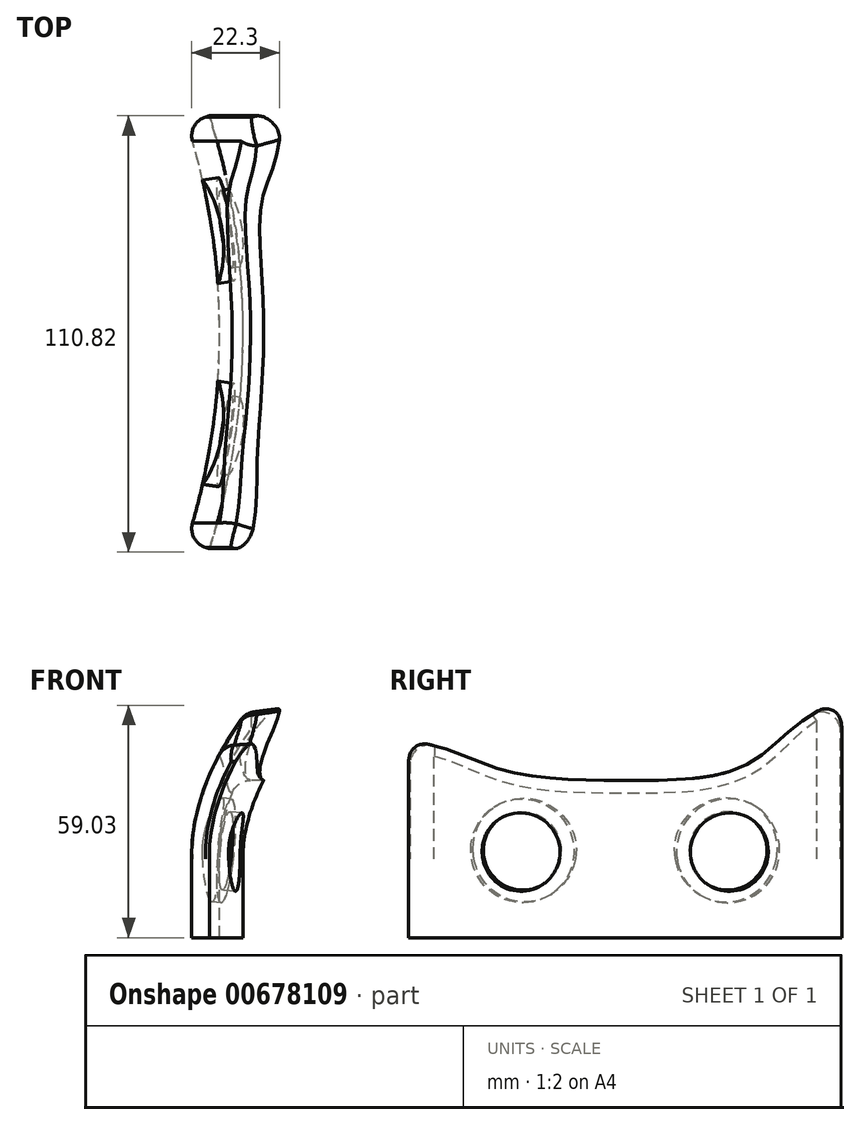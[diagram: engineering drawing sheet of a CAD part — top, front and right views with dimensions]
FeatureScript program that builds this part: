
annotation { "Feature Type Name" : "Feature", "Feature Type Description" : "" }
export const myFeature = defineFeature(function(context is Context, id is Id, definition is map)
    precondition{}
    {
        {
            var Q0;
            Q0=qCreatedBy(makeId("Top.planeOp"),FACE);
            var sketch = newSketch(context, id + "F0", { "sketchPlane" : qUnion([Q0])});
            skCircle(sketch, "E0", {"center": v(0, 0) * mm, "radius": 175 * mm});
            skCircle(sketch, "E1", {"center": v(0, 0) * mm, "radius": 181 * mm});
            skLineSegment(sketch, "E2", {"start": v(0, 0) * mm, "end": v(172.44, 55) * mm});
            skLineSegment(sketch, "E3", {"start": v(0, 0) * mm, "end": v(172.44, -55) * mm});
            skLineSegment(sketch, "E4", {"start": v(172.44, -55) * mm, "end": v(172.44, 55) * mm, "construction": true});
            skPoint(sketch, "E5", {"position": v(175, 0) * mm});
            skLineSegment(sketch, "E6", {"start": v(0, 0) * mm, "end": v(223.4, 0) * mm, "construction": true});
            skPoint(sketch, "E6.endSnap0", {"position": v(172.44, 0) * mm});
            skLineSegment(sketch, "E7", {"start": v(0, 0) * mm, "end": v(293.26, 43.83) * mm, "construction": true});
            skLineSegment(sketch, "E8", {"start": v(0, 0) * mm, "end": v(282.96, -42.29) * mm, "construction": true});
            skLineSegment(sketch, "E9", {"start": v(0, 0) * mm, "end": v(-12.67, 84.8) * mm, "construction": true});
            skLineSegment(sketch, "E10", {"start": v(0, 0) * mm, "end": v(13.6, 91) * mm, "construction": true});
            skSolve(sketch);
        }
        {
            var Q0;
            Q0=qCreatedBy(makeId("Front.planeOp"),FACE);
            var sketch = newSketch(context, id + "F1", { "sketchPlane" : qUnion([Q0])});
            skLineSegment(sketch, "E11.0", {"start": v(-175, 0) * mm, "end": v(175, 0) * mm, "construction": true});
            skLineSegment(sketch, "E12.0", {"start": v(-181, 0) * mm, "end": v(181, 0) * mm, "construction": true});
            skPoint(sketch, "E13.0", {"position": v(172.44, 0) * mm});
            skLineSegment(sketch, "E14", {"start": v(175, 0) * mm, "end": v(181, 0) * mm, "construction": true});
            skPoint(sketch, "E15", {"position": v(178, 0) * mm});
            skFitSpline(sketch, "E16", {"points": [v(178, 0) * mm, v(178, 1.47) * mm, v(203, 45) * mm], "startDerivative": vector(0, 25) * mm, "endDerivative": vector(87.82, 75.46) * mm});
            skLineSegment(sketch, "E17", {"start": v(178, 0) * mm, "end": v(178, 47.04) * mm, "construction": true});
            skLineSegment(sketch, "E18", {"start": v(178, 0) * mm, "end": v(178, -20) * mm, "construction": true});
            skLineSegment(sketch, "E19", {"start": v(178, -20) * mm, "end": v(203, 45) * mm, "construction": true});
            skLineSegment(sketch, "E20", {"start": v(200.37, 20.25) * mm, "end": v(154.68, 20.25) * mm, "construction": true});
            skLineSegment(sketch, "E21", {"start": v(183, 20.25) * mm, "end": v(178, -20) * mm, "construction": true});
            skLineSegment(sketch, "E22", {"start": v(180.5, 0.13) * mm, "end": v(0, 69.55) * mm, "construction": true});
            skLineSegment(sketch, "E23", {"start": v(181, 0) * mm, "end": v(0, 22.5) * mm, "construction": true});
            skLineSegment(sketch, "E24", {"start": v(0, 0) * mm, "end": v(0, 135) * mm, "construction": true});
            skLineSegment(sketch, "E25", {"start": v(0, 0) * mm, "end": v(10.2, 105.85) * mm, "construction": true});
            skLineSegment(sketch, "E26", {"start": v(0, 0) * mm, "end": v(40.9, 106.32) * mm, "construction": true});
            skSolve(sketch);
        }
        {
            var Q0;
            {var subQ0=sQuery(id+"F0.wireOp",EDGE,"E2");var subQ1=sQuery(id+"F0.wireOp",EDGE,"E0");var subQ2=makeQuery(id+"F0.imprint","INTERSECT",VERTEX,{"derivedFrom":[subQ1,subQ0]});Q0=makeQuery(id+"F0.imprint","IMPRINT",FACE,{"disambiguationData":[TD([[makeQuery(id+"F0.imprint","IMPRINT",EDGE,{"disambiguationData":[TD([[subQ2,1.0]])],"derivedFrom":subQ1}),-1.0]])]});}
            var Q1;
            Q1=sQuery(id+"F1.wireOp",EDGE,"E16");
            sweep(context, id + "F2", {"profiles" : qUnion([Q0]), "path" : qUnion([Q1])});
        }
        {
            var Q0;
            Q0=makeQuery(id+"F2.opSweep","SWEPT_EDGE",EDGE,{"disambiguationData":[OSD([sQuery(id+"F0.wireOp",EDGE,"E1"),sQuery(id+"F0.wireOp",EDGE,"E3"),sQuery(id+"F1.wireOp",EDGE,"E16")])]});
            cPoint(context, id + "F3", {"entities" : qUnion([Q0]), "parameter" : 0.5});
        }
        {
            var Q0;
            Q0=qCreatedBy(makeId("Front.planeOp"),FACE);
            var Q1;
            Q1=qCreatedBy(id+"F3",VERTEX);
            cPlane(context, id + "F4", {"entities" : qUnion([Q0, Q1]), "cplaneType" : CPlaneType.PLANE_POINT, "offset" : 25 * mm, "width" : 150 * mm, "height" : 150 * mm});
        }
        {
            var Q0;
            Q0=qCreatedBy(id+"F4.planeOp",FACE);
            var sketch = newSketch(context, id + "F5", { "sketchPlane" : qUnion([Q0])});
            skLineSegment(sketch, "E27", {"start": v(16.14, 30) * mm, "end": v(342.74, 30) * mm});
            skLineSegment(sketch, "E28.top", {"start": v(16.14, 180) * mm, "end": v(342.74, 180) * mm});
            skLineSegment(sketch, "E28.left", {"start": v(16.14, 30) * mm, "end": v(16.14, 180) * mm});
            skLineSegment(sketch, "E28.right", {"start": v(342.74, 30) * mm, "end": v(342.74, 180) * mm});
            skSolve(sketch);
        }
        {
            var Q0;
            Q0=qCreatedBy(makeId("Right.planeOp"),FACE);
            var sketch = newSketch(context, id + "F6", { "sketchPlane" : qUnion([Q0])});
            skPoint(sketch, "E29.0", {"position": v(-55, 30) * mm});
            skLineSegment(sketch, "E30", {"start": v(-74, 30) * mm, "end": v(-141.5, 30) * mm, "construction": true});
            skFitSpline(sketch, "E31.0", {"points": [v(55, 0) * mm, v(1000, 55) * mm, v(1.76, 1000) * mm, v(55, 1.45) * mm, v(1000, 55) * mm, v(2.22, 1000) * mm, v(55, 2.64) * mm, v(1000, 55) * mm, v(3.74, 1000) * mm, v(55, 4.43) * mm, v(1000, 55) * mm, v(6.86, 1000) * mm, v(55, 8.96) * mm, v(1000, 55) * mm, v(16.48, 1000) * mm, v(55, 23.08) * mm], "construction": true});
            skFitSpline(sketch, "E32.0", {"points": [v(-55, 0) * mm, v(1000, -55) * mm, v(1.76, 1000) * mm, v(-55, 1.45) * mm, v(1000, -55) * mm, v(2.22, 1000) * mm, v(-55, 2.64) * mm, v(1000, -55) * mm, v(3.74, 1000) * mm, v(-55, 4.43) * mm, v(1000, -55) * mm, v(6.86, 1000) * mm, v(-55, 8.96) * mm, v(1000, -55) * mm, v(16.48, 1000) * mm, v(-55, 23.08) * mm], "construction": true});
            skLineSegment(sketch, "E33", {"start": v(68.45, 40) * mm, "end": v(-5.43, 40) * mm, "construction": true});
            skLineSegment(sketch, "E34", {"start": v(28.07, 20) * mm, "end": v(-24.08, 20) * mm, "construction": true});
            skFitSpline(sketch, "E35", {"points": [v(55, 40) * mm, v(31.56, 24.33) * mm, v(0, 20) * mm, v(-30.54, 22.45) * mm, v(-55, 30) * mm], "startDerivative": vector(-142.73, -39.4) * mm, "endDerivative": vector(-137.35, 16.17) * mm});
            skSolve(sketch);
        }
        {
            var Q0;
            Q0=makeQuery(id+"F5.imprint","IMPRINT",FACE,{"disambiguationData":[TD([[makeQuery(id+"F5.imprint","IMPRINT",EDGE,{"derivedFrom":sQuery(id+"F5.wireOp",EDGE,"E27")}),1.0]])]});
            var Q1;
            Q1=sQuery(id+"F6.wireOp",EDGE,"E35");
            sweep(context, id + "F7", {"operationType" : NewBodyOperationType.REMOVE, "profiles" : qUnion([Q0]), "path" : qUnion([Q1]), "keepProfileOrientation" : true});
        }
        {
            var Q0;
            Q0=makeQuery(id+"F7.boolean.opBoolean","INTERSECT",EDGE,{"derivedFrom":[makeQuery(id+"F2.opSweep","SWEPT_FACE",FACE,{"disambiguationData":[OSD([sQuery(id+"F0.wireOp",EDGE,"E0"),sQuery(id+"F1.wireOp",EDGE,"E16")])]}),makeQuery(id+"F7.opSweep","SWEPT_FACE",FACE,{"disambiguationData":[OSD([sQuery(id+"F5.wireOp",EDGE,"E27"),sQuery(id+"F6.wireOp",EDGE,"E35")])]})]});
            fillet(context, id + "F8", {"entities" : qUnion([Q0]), "radius" : 5 * mm, "tangentPropagation" : true, "allowEdgeOverflow" : false});
        }
        {
            var Q0;
            Q0=makeQuery(id+"F2.opSweep","SWEPT_EDGE",EDGE,{"disambiguationData":[OSD([sQuery(id+"F0.wireOp",EDGE,"E0"),sQuery(id+"F0.wireOp",EDGE,"E2"),sQuery(id+"F1.wireOp",EDGE,"E16")])]});
            var Q1;
            Q1=makeQuery(id+"F2.opSweep","SWEPT_EDGE",EDGE,{"disambiguationData":[OSD([sQuery(id+"F0.wireOp",EDGE,"E0"),sQuery(id+"F0.wireOp",EDGE,"E3"),sQuery(id+"F1.wireOp",EDGE,"E16")])]});
            fillet(context, id + "F9", {"entities" : qUnion([Q0, Q1]), "radius" : 5 * mm, "tangentPropagation" : true, "allowEdgeOverflow" : false});
        }
        {
            var Q0;
            Q0=makeQuery(id+"F2.opSweep","CAP_FACE",FACE,{"disambiguationData":[OSD([sQuery(id+"F0.wireOp",EDGE,"E0"),sQuery(id+"F0.wireOp",EDGE,"E1"),sQuery(id+"F0.wireOp",EDGE,"E2"),sQuery(id+"F0.wireOp",EDGE,"E3"),sQuery(id+"F1.wireOp",VERTEX,"E16.start")])],"isStart":true});
            var sketch = newSketch(context, id + "F10", { "sketchPlane" : qUnion([Q0])});
            skLineSegment(sketch, "E36.0.0", {"start": v(172.44, 55) * mm, "end": v(171.42, 54.68) * mm});
            skArc(sketch, "E36.0.1", {"start": v(171.42, 54.68) * mm, "mid": v(168.53, 52.27) * mm, "end": v(168.14, 48.53) * mm});
            skArc(sketch, "E36.0.2", {"start": v(168.14, -48.53) * mm, "mid": v(175, 0) * mm, "end": v(168.14, 48.53) * mm});
            skArc(sketch, "E36.0.3", {"start": v(168.14, -48.53) * mm, "mid": v(168.53, -52.27) * mm, "end": v(171.42, -54.68) * mm});
            skLineSegment(sketch, "E36.0.4", {"start": v(172.44, -55) * mm, "end": v(171.42, -54.68) * mm});
            skArc(sketch, "E36.0.5", {"start": v(172.44, -55) * mm, "mid": v(181, 0) * mm, "end": v(172.44, 55) * mm});
            skSolve(sketch);
        }
        {
            var Q0;
            Q0=makeQuery(id+"F10.imprint","IMPRINT",FACE,{"disambiguationData":[TD([[makeQuery(id+"F10.imprint","IMPRINT",EDGE,{"derivedFrom":sQuery(id+"F10.wireOp",EDGE,"E36.0.0")}),-1.0]])]});
            extrude(context, id + "F11", {"entities" : qUnion([Q0]), "operationType" : NewBodyOperationType.ADD, "depth" : 20 * mm, "offsetDistance" : 25 * mm, "hasSecondDirection" : true, "secondDirectionOppositeDirection" : true, "secondDirectionDepth" : 1 * mm});
        }
        {
            var Q0;
            Q0=sQuery(id+"F0.wireOp",VERTEX,"E9.end");
            var Q1;
            Q1=sQuery(id+"F0.wireOp",VERTEX,"E2.start");
            var Q2;
            Q2=sQuery(id+"F1.wireOp",VERTEX,"E25.end");
            cPlane(context, id + "F12", {"entities" : qUnion([Q0, Q1, Q2]), "cplaneType" : CPlaneType.THREE_POINT, "offset" : 25 * mm, "width" : 150 * mm, "height" : 150 * mm});
        }
        {
            var Q0;
            Q0=sQuery(id+"F0.wireOp",VERTEX,"E10.end");
            var Q1;
            Q1=sQuery(id+"F1.wireOp",VERTEX,"E25.end");
            var Q2;
            Q2=sQuery(id+"F0.wireOp",VERTEX,"E2.start");
            cPlane(context, id + "F13", {"entities" : qUnion([Q0, Q1, Q2]), "cplaneType" : CPlaneType.THREE_POINT, "offset" : 25 * mm, "width" : 150 * mm, "height" : 150 * mm});
        }
        {
            var Q0;
            Q0=qCreatedBy(id+"F12.planeOp",FACE);
            var sketch = newSketch(context, id + "F14", { "sketchPlane" : qUnion([Q0])});
            skCircle(sketch, "E37", {"center": v(0, 19) * mm, "radius": 10 * mm});
            skCircle(sketch, "E38", {"center": v(0, 19) * mm, "radius": 13.25 * mm});
            skSolve(sketch);
        }
        {
            var Q0;
            Q0=qCreatedBy(id+"F13.planeOp",FACE);
            var sketch = newSketch(context, id + "F15", { "sketchPlane" : qUnion([Q0])});
            skCircle(sketch, "E39", {"center": v(0, 19) * mm, "radius": 10 * mm});
            skCircle(sketch, "E40", {"center": v(0, 19) * mm, "radius": 13.25 * mm});
            skSolve(sketch);
        }
        {
            var Q0;
            Q0=makeQuery(id+"F14.imprint","IMPRINT",FACE,{"disambiguationData":[TD([[makeQuery(id+"F14.imprint","IMPRINT",EDGE,{"derivedFrom":sQuery(id+"F14.wireOp",EDGE,"E37")}),1.0]])]});
            var Q1;
            Q1=makeQuery(id+"F2.opSweep","SWEPT_BODY",BODY,{"disambiguationData":[OSD([sQuery(id+"F0.wireOp",EDGE,"E0"),sQuery(id+"F0.wireOp",EDGE,"E1"),sQuery(id+"F0.wireOp",EDGE,"E2"),sQuery(id+"F0.wireOp",EDGE,"E3"),sQuery(id+"F1.wireOp",EDGE,"E16")])]});
            extrude(context, id + "F16", {"entities" : qUnion([Q0]), "operationType" : NewBodyOperationType.REMOVE, "endBound" : BoundingType.UP_TO_BODY, "depth" : 25 * mm, "endBoundEntityBody" : qUnion([Q1]), "hasOffset" : true, "offsetDistance" : 10 * mm, "offsetOppositeDirection" : true});
        }
        {
            var Q0;
            Q0=makeQuery(id+"F15.imprint","IMPRINT",FACE,{"disambiguationData":[TD([[makeQuery(id+"F15.imprint","IMPRINT",EDGE,{"derivedFrom":sQuery(id+"F15.wireOp",EDGE,"E39")}),1.0]])]});
            var Q1;
            Q1=makeQuery(id+"F2.opSweep","SWEPT_BODY",BODY,{"disambiguationData":[OSD([sQuery(id+"F0.wireOp",EDGE,"E0"),sQuery(id+"F0.wireOp",EDGE,"E1"),sQuery(id+"F0.wireOp",EDGE,"E2"),sQuery(id+"F0.wireOp",EDGE,"E3"),sQuery(id+"F1.wireOp",EDGE,"E16")])]});
            extrude(context, id + "F17", {"entities" : qUnion([Q0]), "operationType" : NewBodyOperationType.REMOVE, "endBound" : BoundingType.UP_TO_BODY, "oppositeDirection" : true, "depth" : 25 * mm, "endBoundEntityBody" : qUnion([Q1]), "hasOffset" : true, "offsetDistance" : 10 * mm, "offsetOppositeDirection" : true});
        }
        {
            var Q0;
            Q0=makeQuery(id+"F14.imprint","IMPRINT",FACE,{"disambiguationData":[TD([[makeQuery(id+"F14.imprint","IMPRINT",EDGE,{"derivedFrom":sQuery(id+"F14.wireOp",EDGE,"E37")}),-1.0]])]});
            var Q1;
            Q1=makeQuery(id+"F2.opSweep","SWEPT_FACE",FACE,{"disambiguationData":[OSD([sQuery(id+"F0.wireOp",EDGE,"E0"),sQuery(id+"F1.wireOp",EDGE,"E16")])]});
            var Q2;
            Q2=makeQuery(id+"F2.opSweep","SWEPT_BODY",BODY,{"disambiguationData":[OSD([sQuery(id+"F0.wireOp",EDGE,"E0"),sQuery(id+"F0.wireOp",EDGE,"E1"),sQuery(id+"F0.wireOp",EDGE,"E2"),sQuery(id+"F0.wireOp",EDGE,"E3"),sQuery(id+"F1.wireOp",EDGE,"E16")])]});
            extrude(context, id + "F18", {"entities" : qUnion([Q0]), "operationType" : NewBodyOperationType.REMOVE, "depth" : (173.6 + 4) * mm, "endBoundEntityFace" : qUnion([Q1]), "endBoundEntityBody" : qUnion([Q2]), "hasOffset" : true, "offsetDistance" : 3 * mm, "offsetOppositeDirection" : true});
        }
        {
            var Q0;
            Q0=makeQuery(id+"F15.imprint","IMPRINT",FACE,{"disambiguationData":[TD([[makeQuery(id+"F15.imprint","IMPRINT",EDGE,{"derivedFrom":sQuery(id+"F15.wireOp",EDGE,"E39")}),-1.0]])]});
            var Q1;
            Q1=makeQuery(id+"F2.opSweep","SWEPT_BODY",BODY,{"disambiguationData":[OSD([sQuery(id+"F0.wireOp",EDGE,"E0"),sQuery(id+"F0.wireOp",EDGE,"E1"),sQuery(id+"F0.wireOp",EDGE,"E2"),sQuery(id+"F0.wireOp",EDGE,"E3"),sQuery(id+"F1.wireOp",EDGE,"E16")])]});
            extrude(context, id + "F19", {"entities" : qUnion([Q0]), "operationType" : NewBodyOperationType.REMOVE, "oppositeDirection" : true, "depth" : (173.6 + 4) * mm, "endBoundEntityBody" : qUnion([Q1]), "hasOffset" : true, "offsetDistance" : 3 * mm, "offsetOppositeDirection" : true});
        }
    });
